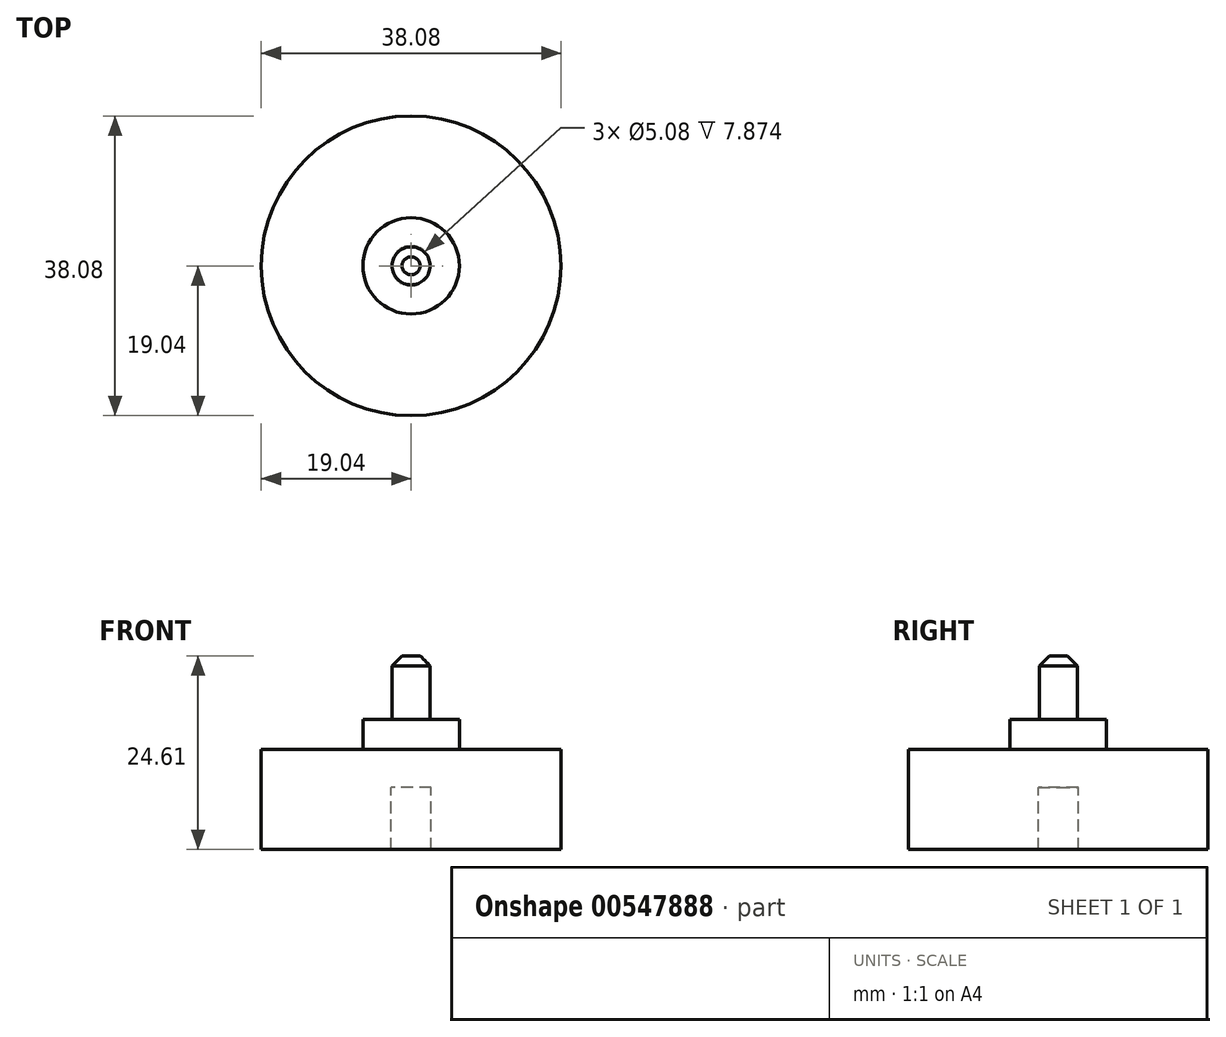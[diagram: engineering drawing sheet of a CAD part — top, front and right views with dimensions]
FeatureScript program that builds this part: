
annotation { "Feature Type Name" : "Feature", "Feature Type Description" : "" }
export const myFeature = defineFeature(function(context is Context, id is Id, definition is map)
    precondition{}
    {
        {
            var Q0;
            Q0=qCreatedBy(makeId("Front.planeOp"),FACE);
            var sketch = newSketch(context, id + "F0", { "sketchPlane" : qUnion([Q0])});
            skLineSegment(sketch, "E0", {"start": v(19.04, 0) * mm, "end": v(19.04, 12.7) * mm});
            skLineSegment(sketch, "E1", {"start": v(6.12, 16.51) * mm, "end": v(6.12, 12.7) * mm});
            skPoint(sketch, "E1.endSnap0", {"position": v(9.52, 12.7) * mm});
            skLineSegment(sketch, "E2", {"start": v(19.04, 12.7) * mm, "end": v(6.12, 12.7) * mm});
            skLineSegment(sketch, "E3", {"start": v(2.54, 0) * mm, "end": v(2.54, 7.87) * mm});
            skLineSegment(sketch, "E4", {"start": v(2.54, 7.87) * mm, "end": v(0, 7.87) * mm});
            skLineSegment(sketch, "E5", {"start": v(0, 24.61) * mm, "end": v(0, 7.87) * mm});
            skLineSegment(sketch, "E6", {"start": v(19.04, 0) * mm, "end": v(2.54, 0) * mm});
            skLineSegment(sketch, "E7", {"start": v(0, 24.61) * mm, "end": v(2.41, 24.61) * mm});
            skLineSegment(sketch, "E8", {"start": v(2.41, 24.61) * mm, "end": v(2.41, 16.51) * mm});
            skLineSegment(sketch, "E9", {"start": v(6.12, 16.51) * mm, "end": v(2.41, 16.51) * mm});
            skSolve(sketch);
        }
        {
            var Q0;
            Q0 = qSketchRegion(id + "F0", true);
            var Q1;
            Q1=sQuery(id+"F0.wireOp",EDGE,"E5");
            revolve(context, id + "F1", {"entities" : qUnion([Q0]), "axis" : qUnion([Q1]), "revolveType" : RevolveType.FULL});
        }
        {
            var Q0;
            Q0=makeQuery(id+"F1.opRevolve","SWEPT_EDGE",EDGE,{"disambiguationData":[OSD([sQuery(id+"F0.wireOp",EDGE,"E7"),sQuery(id+"F0.wireOp",EDGE,"E8")])]});
            chamfer(context, id + "F2", {"entities" : qUnion([Q0]), "width" : 1.27 * mm, "tangentPropagation" : true});
        }
    });
